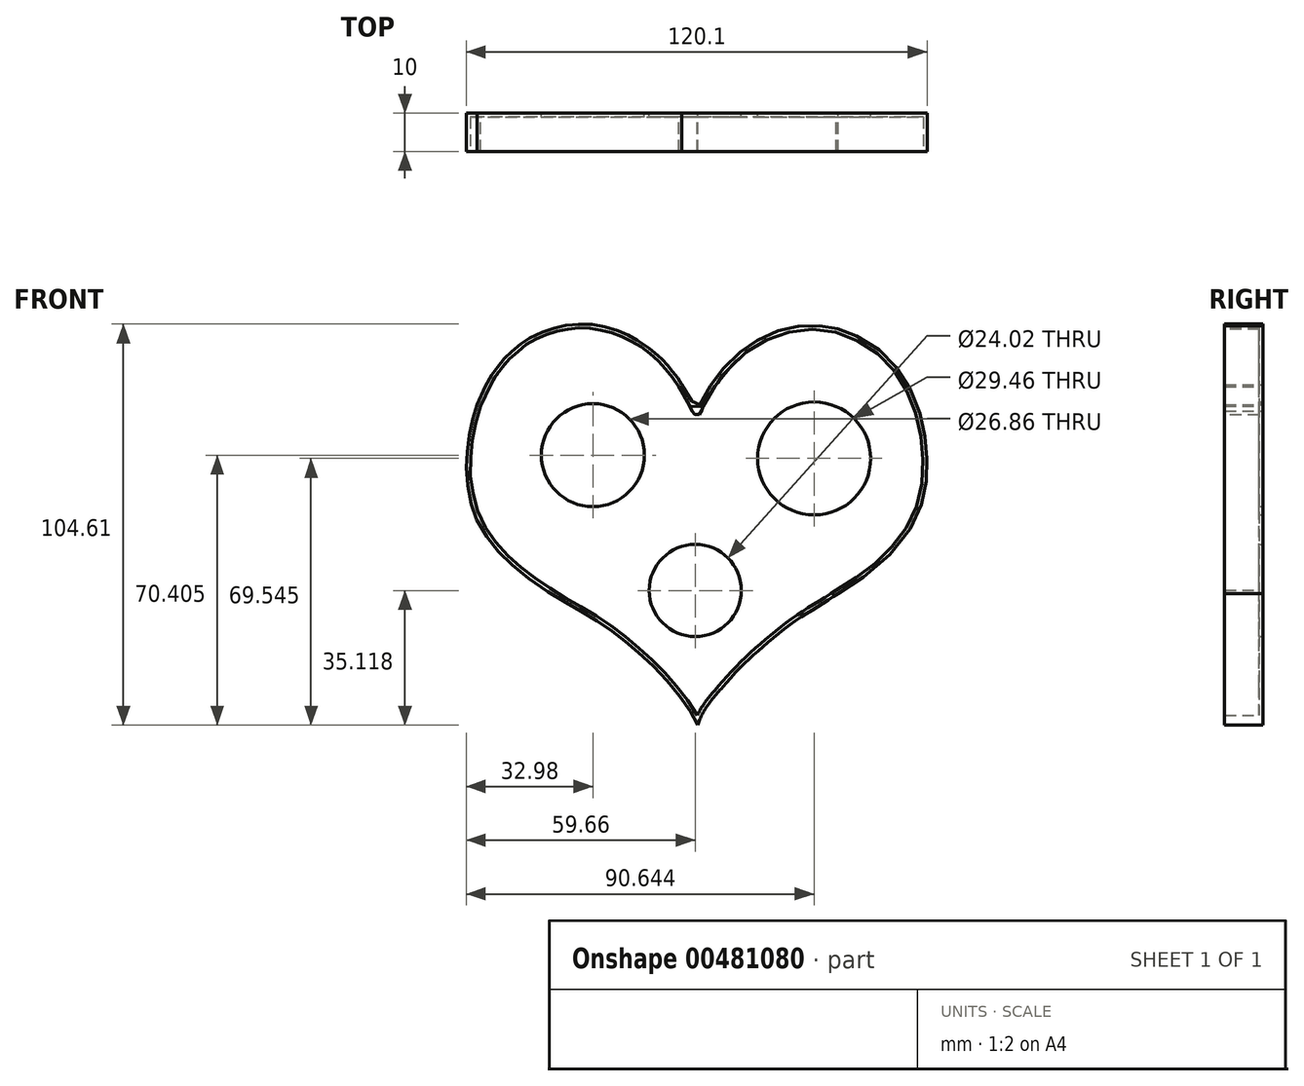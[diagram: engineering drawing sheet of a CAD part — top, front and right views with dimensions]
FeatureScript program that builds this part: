
annotation { "Feature Type Name" : "Feature", "Feature Type Description" : "" }
export const myFeature = defineFeature(function(context is Context, id is Id, definition is map)
    precondition{}
    {
        {
            var Q0;
            Q0=qCreatedBy(makeId("Front.planeOp"),FACE);
            var sketch = newSketch(context, id + "F0", { "sketchPlane" : qUnion([Q0])});
            skFitSpline(sketch, "E0", {"points": [v(6.73, -45.3) * mm, v(11.84, -39.7) * mm, v(16.02, -35.76) * mm, v(21.21, -31.33) * mm, v(26.99, -26.97) * mm, v(32.51, -23.46) * mm, v(37.29, -20.44) * mm], "startDerivative": vector(29.23, 33.13) * mm, "endDerivative": vector(30.32, 19.32) * mm});
            skFitSpline(sketch, "E1", {"points": [v(37.29, -20.44) * mm, v(42.66, -17.02) * mm, v(48.91, -12.09) * mm, v(54.88, -5.35) * mm, v(57.6, -0.7) * mm, v(59.33, 4.16) * mm, v(60.1, 7.85) * mm, v(60.44, 12.15) * mm, v(60.3, 15.48) * mm, v(60.03, 19.08) * mm, v(59.64, 22.13) * mm, v(58.54, 26.47) * mm, v(56.85, 31.01) * mm, v(54.65, 35.36) * mm, v(51.8, 39.25) * mm, v(48.94, 42.3) * mm, v(44.45, 45.46) * mm, v(41.07, 47.18) * mm, v(38.4, 48.2) * mm, v(35.72, 48.9) * mm, v(33.47, 49.26) * mm, v(30.85, 49.44) * mm, v(27.23, 49.26) * mm, v(24.14, 48.72) * mm, v(21.11, 47.9) * mm, v(17.6, 46.29) * mm, v(14.58, 44.69) * mm, v(12.15, 42.9) * mm, v(9.06, 39.94) * mm, v(6.68, 37.5) * mm, v(4.84, 34.95) * mm, v(2.76, 31.98) * mm, v(1.28, 29.13) * mm, v(0.45, 27.17) * mm, v(-0.74, 29.36) * mm, v(-2.05, 31.86) * mm, v(-3.47, 34) * mm], "startDerivative": vector(148.93, 91.73) * mm, "endDerivative": vector(-65.08, 94.72) * mm});
            skFitSpline(sketch, "E2", {"points": [v(-3.47, 34) * mm, v(-4.35, 35.43) * mm, v(-5.42, 36.87) * mm, v(-6.43, 38.11) * mm, v(-7.45, 39.33) * mm, v(-8.58, 40.5) * mm, v(-9.46, 41.41) * mm, v(-9.82, 41.74) * mm, v(-13, 44.32) * mm, v(-16.55, 46.4) * mm, v(-18.94, 47.58) * mm, v(-23.02, 48.92) * mm, v(-27.36, 49.75) * mm, v(-31.92, 49.7) * mm, v(-35.87, 49) * mm, v(-39.25, 47.97) * mm, v(-43.6, 45.97) * mm, v(-45.98, 44.2) * mm, v(-48.8, 41.8) * mm, v(-50.15, 40.37) * mm, v(-52.36, 37.5) * mm, v(-53.4, 36.07) * mm, v(-56.86, 28.82) * mm], "startDerivative": vector(-23.97, 41.45) * mm, "endDerivative": vector(-52.85, -117.21) * mm});
            skFitSpline(sketch, "E3", {"points": [v(-56.86, 28.82) * mm, v(-58.11, 24.57) * mm, v(-59.1, 19.74) * mm, v(-59.54, 14.96) * mm, v(-59.6, 10.03) * mm, v(-58.52, 3.59) * mm, v(-56.86, -1.36) * mm, v(-53.06, -7.4) * mm, v(-48.85, -11.98) * mm, v(-42.28, -17.3) * mm, v(-34.68, -22.24) * mm, v(-29.67, -25.19) * mm, v(-24.23, -28.5) * mm, v(-19.62, -31.78) * mm, v(-15.67, -35.13) * mm, v(-10.31, -39.97) * mm, v(-5.48, -45.47) * mm, v(-1.53, -50.76) * mm, v(0.68, -54.77) * mm], "startDerivative": vector(-27.36, -87.87) * mm, "endDerivative": vector(40.96, -81.15) * mm});
            skFitSpline(sketch, "E4", {"points": [v(0.68, -54.77) * mm, v(1.72, -52.07) * mm, v(4.26, -48.25) * mm, v(6.73, -45.3) * mm], "startDerivative": vector(2.75, 8.85) * mm, "endDerivative": vector(7.18, 8.22) * mm});
            skSolve(sketch);
        }
        {
            var Q0;
            Q0=makeQuery(id+"F0.imprint","IMPRINT",FACE,{"disambiguationData":[TD([[makeQuery(id+"F0.imprint","IMPRINT",EDGE,{"derivedFrom":sQuery(id+"F0.wireOp",EDGE,"E0")}),1.0]])]});
            extrude(context, id + "F1", {"entities" : qUnion([Q0]), "depth" : 10 * mm});
        }
        {
            var Q0;
            Q0=makeQuery(id+"F1.opExtrude","CAP_FACE",FACE,{"disambiguationData":[OSD([sQuery(id+"F0.wireOp",EDGE,"E0"),sQuery(id+"F0.wireOp",EDGE,"E1"),sQuery(id+"F0.wireOp",EDGE,"E2"),sQuery(id+"F0.wireOp",EDGE,"E3"),sQuery(id+"F0.wireOp",EDGE,"E4")])],"isStart":false});
            shell(context, id + "F2", {"entities" : qUnion([Q0]), "thickness" : 1 * mm});
        }
        {
            var Q0;
            Q0=makeQuery(id+"F2.opShell","OFFSET_FACE",FACE,{"disambiguationData":[OSD([sQuery(id+"F0.wireOp",EDGE,"E0"),sQuery(id+"F0.wireOp",EDGE,"E1"),sQuery(id+"F0.wireOp",EDGE,"E2"),sQuery(id+"F0.wireOp",EDGE,"E3"),sQuery(id+"F0.wireOp",EDGE,"E4")])]});
            var sketch = newSketch(context, id + "F3", { "sketchPlane" : qUnion([Q0])});
            skCircle(sketch, "E5", {"center": v(-33.87, 19.5) * mm, "radius": 13.5 * mm});
            skCircle(sketch, "E6", {"center": v(31.03, 17.42) * mm, "radius": 13.6 * mm});
            skCircle(sketch, "E7", {"center": v(0, -19.5) * mm, "radius": 12.49 * mm});
            skSolve(sketch);
        }
        {
            var Q0;
            Q0=makeQuery(id+"F3.imprint","IMPRINT",FACE,{"disambiguationData":[TD([[makeQuery(id+"F3.imprint","IMPRINT",EDGE,{"derivedFrom":sQuery(id+"F3.wireOp",EDGE,"E5")}),1.0]])]});
            var Q1;
            Q1=makeQuery(id+"F3.imprint","IMPRINT",FACE,{"disambiguationData":[TD([[makeQuery(id+"F3.imprint","IMPRINT",EDGE,{"derivedFrom":sQuery(id+"F3.wireOp",EDGE,"E6")}),1.0]])]});
            var Q2;
            Q2=makeQuery(id+"F3.imprint","IMPRINT",FACE,{"disambiguationData":[TD([[makeQuery(id+"F3.imprint","IMPRINT",EDGE,{"derivedFrom":sQuery(id+"F3.wireOp",EDGE,"E7")}),1.0]])]});
            extrude(context, id + "F4", {"entities" : qUnion([Q0, Q1, Q2]), "operationType" : NewBodyOperationType.REMOVE, "depth" : 30 * mm});
        }
        {
            var Q0;
            Q0=qCreatedBy(makeId("Front.planeOp"),FACE);
            var sketch = newSketch(context, id + "F5", { "sketchPlane" : qUnion([Q0])});
            skCircle(sketch, "E8", {"center": v(-26.68, 15.64) * mm, "radius": 13.43 * mm});
            skCircle(sketch, "E9", {"center": v(30.98, 14.77) * mm, "radius": 14.73 * mm});
            skCircle(sketch, "E10", {"center": v(0, -19.65) * mm, "radius": 12.01 * mm});
            skSolve(sketch);
        }
        {
            var Q0;
            Q0 = qSketchRegion(id + "F5", true);
            extrude(context, id + "F6", {"entities" : qUnion([Q0]), "operationType" : NewBodyOperationType.REMOVE, "oppositeDirection" : true, "depth" : 25 * mm});
        }
        {
            var Q0;
            Q0 = qSketchRegion(id + "F5", true);
            extrude(context, id + "F7", {"entities" : qUnion([Q0]), "operationType" : NewBodyOperationType.REMOVE, "endBound" : BoundingType.THROUGH_ALL, "depth" : 25 * mm});
        }
    });
